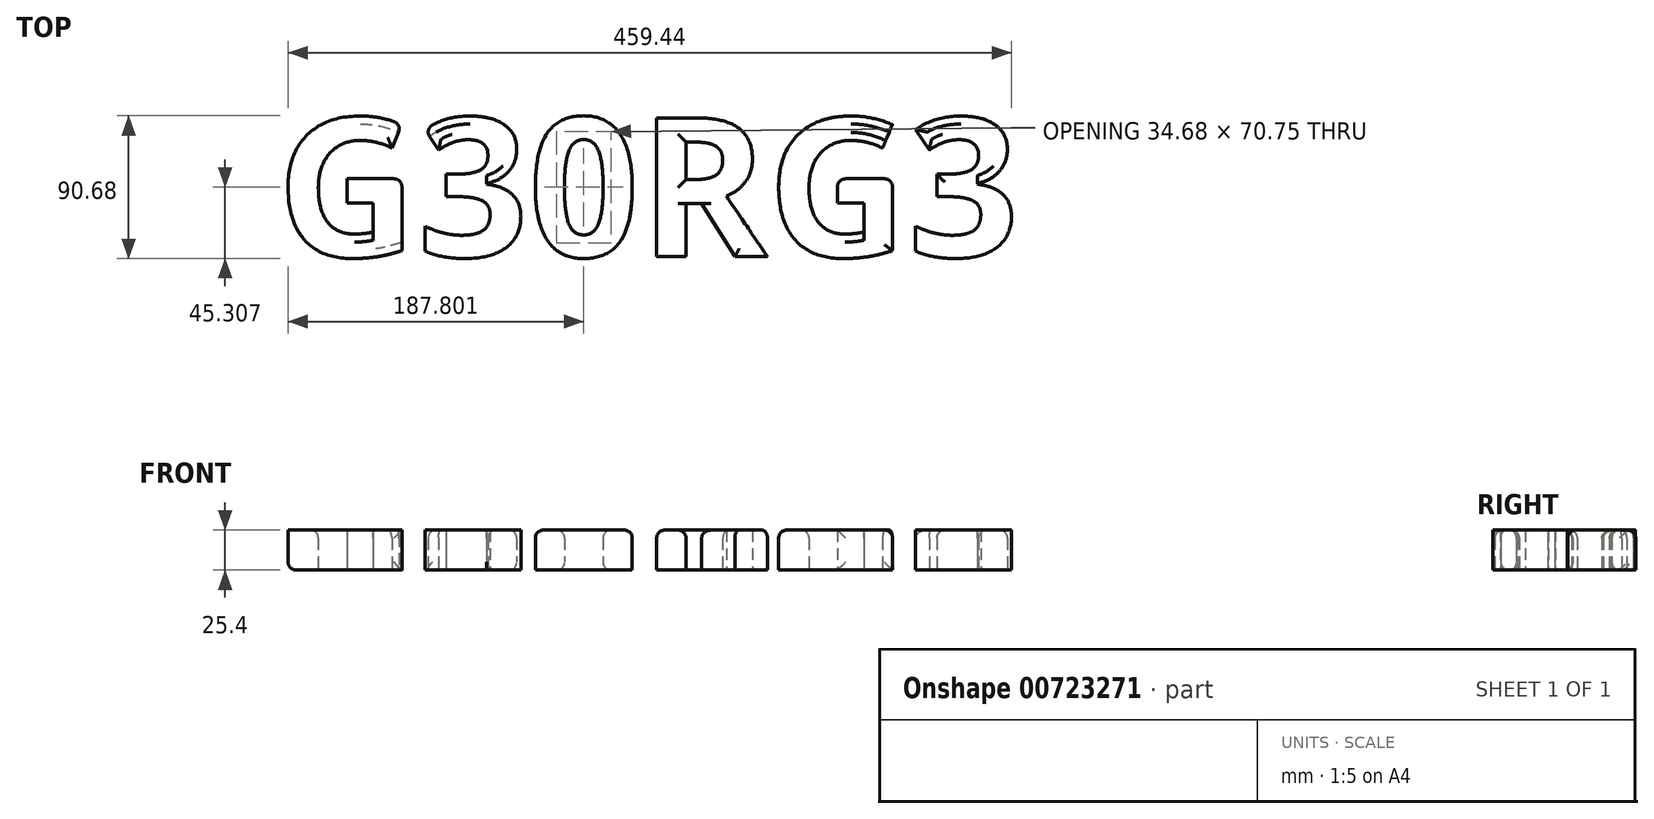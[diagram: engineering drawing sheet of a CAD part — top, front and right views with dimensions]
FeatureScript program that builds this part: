
annotation { "Feature Type Name" : "Feature", "Feature Type Description" : "" }
export const myFeature = defineFeature(function(context is Context, id is Id, definition is map)
    precondition{}
    {
        {
            var Q0;
            Q0=qCreatedBy(makeId("Top.planeOp"),FACE);
            var sketch = newSketch(context, id + "F0", { "sketchPlane" : qUnion([Q0])});
            skText(sketch, "E0", { "text": "G30RG3", "fontName": "OpenSans-Bold.ttf"});
            const initialGuessF0  = {"E0": [-0.20131, -0.08418, 1, 0, 0.08883]};
            skSetInitialGuess(sketch, initialGuessF0);
            skSolve(sketch);
        }
        {
            var Q0;
            Q0 = qSketchRegion(id + "F0", true);
            extrude(context, id + "F1", {"entities" : qUnion([Q0]), "depth" : 25.4 * mm, "offsetDistance" : 25.4 * mm});
        }
        {
            var Q0;
            Q0=makeQuery(id+"F1.opExtrude","CAP_EDGE",EDGE,{"disambiguationData":[OSD([sQuery(id+"F0.wireOp",EDGE,"E0.sketch_text.stroke-9")])],"isStart":false});
            var Q1;
            Q1=makeQuery(id+"F1.opExtrude","SWEPT_EDGE",EDGE,{"disambiguationData":[OSD([sQuery(id+"F0.wireOp",EDGE,"E0.sketch_text.stroke-8"),sQuery(id+"F0.wireOp",EDGE,"E0.sketch_text.stroke-9")])]});
            var Q2;
            Q2=makeQuery(id+"F1.opExtrude","CAP_EDGE",EDGE,{"disambiguationData":[OSD([sQuery(id+"F0.wireOp",EDGE,"E0.sketch_text.stroke-8")])],"isStart":true});
            var Q3;
            Q3=makeQuery(id+"F1.opExtrude","CAP_EDGE",EDGE,{"disambiguationData":[OSD([sQuery(id+"F0.wireOp",EDGE,"E0.sketch_text.stroke-10")])],"isStart":false});
            var Q4;
            Q4=makeQuery(id+"F1.opExtrude","CAP_EDGE",EDGE,{"disambiguationData":[OSD([sQuery(id+"F0.wireOp",EDGE,"E0.sketch_text.stroke-43")])],"isStart":false});
            var Q5;
            Q5=makeQuery(id+"F1.opExtrude","SWEPT_EDGE",EDGE,{"disambiguationData":[OSD([sQuery(id+"F0.wireOp",EDGE,"E0.sketch_text.stroke-42"),sQuery(id+"F0.wireOp",EDGE,"E0.sketch_text.stroke-43")])]});
            var Q6;
            Q6=makeQuery(id+"F1.opExtrude","CAP_EDGE",EDGE,{"disambiguationData":[OSD([sQuery(id+"F0.wireOp",EDGE,"E0.sketch_text.stroke-43")])],"isStart":true});
            var Q7;
            Q7=makeQuery(id+"F1.opExtrude","CAP_EDGE",EDGE,{"disambiguationData":[OSD([sQuery(id+"F0.wireOp",EDGE,"E0.sketch_text.stroke-42")])],"isStart":false});
            var Q8;
            Q8=makeQuery(id+"F1.opExtrude","CAP_EDGE",EDGE,{"disambiguationData":[OSD([sQuery(id+"F0.wireOp",EDGE,"E0.sketch_text.stroke-41")])],"isStart":false});
            var Q9;
            Q9=makeQuery(id+"F1.opExtrude","CAP_EDGE",EDGE,{"disambiguationData":[OSD([sQuery(id+"F0.wireOp",EDGE,"E0.sketch_text.stroke-0")])],"isStart":false});
            var Q10;
            Q10=makeQuery(id+"F1.opExtrude","CAP_EDGE",EDGE,{"disambiguationData":[OSD([sQuery(id+"F0.wireOp",EDGE,"E0.sketch_text.stroke-0")])],"isStart":true});
            var Q11;
            Q11=makeQuery(id+"F1.opExtrude","SWEPT_EDGE",EDGE,{"disambiguationData":[OSD([sQuery(id+"F0.wireOp",EDGE,"E0.sketch_text.stroke-0"),sQuery(id+"F0.wireOp",EDGE,"E0.sketch_text.stroke-1")])]});
            var Q12;
            Q12=makeQuery(id+"F1.opExtrude","CAP_EDGE",EDGE,{"disambiguationData":[OSD([sQuery(id+"F0.wireOp",EDGE,"E0.sketch_text.stroke-55")])],"isStart":false});
            var Q13;
            Q13=makeQuery(id+"F1.opExtrude","CAP_EDGE",EDGE,{"disambiguationData":[OSD([sQuery(id+"F0.wireOp",EDGE,"E0.sketch_text.stroke-55")])],"isStart":true});
            var Q14;
            Q14=makeQuery(id+"F1.opExtrude","CAP_EDGE",EDGE,{"disambiguationData":[OSD([sQuery(id+"F0.wireOp",EDGE,"E0.sketch_text.stroke-51")])],"isStart":false});
            var Q15;
            Q15=makeQuery(id+"F1.opExtrude","CAP_EDGE",EDGE,{"disambiguationData":[OSD([sQuery(id+"F0.wireOp",EDGE,"E0.sketch_text.stroke-52")])],"isStart":false});
            var Q16;
            Q16=makeQuery(id+"F1.opExtrude","CAP_EDGE",EDGE,{"disambiguationData":[OSD([sQuery(id+"F0.wireOp",EDGE,"E0.sketch_text.stroke-62")])],"isStart":false});
            var Q17;
            Q17=makeQuery(id+"F1.opExtrude","CAP_EDGE",EDGE,{"disambiguationData":[OSD([sQuery(id+"F0.wireOp",EDGE,"E0.sketch_text.stroke-68")])],"isStart":false});
            var Q18;
            Q18=makeQuery(id+"F1.opExtrude","CAP_EDGE",EDGE,{"disambiguationData":[OSD([sQuery(id+"F0.wireOp",EDGE,"E0.sketch_text.stroke-71")])],"isStart":false});
            var Q19;
            Q19=makeQuery(id+"F1.opExtrude","CAP_EDGE",EDGE,{"disambiguationData":[OSD([sQuery(id+"F0.wireOp",EDGE,"E0.sketch_text.stroke-69")])],"isStart":false});
            var Q20;
            Q20=makeQuery(id+"F1.opExtrude","CAP_EDGE",EDGE,{"disambiguationData":[OSD([sQuery(id+"F0.wireOp",EDGE,"E0.sketch_text.stroke-79")])],"isStart":false});
            var Q21;
            Q21=makeQuery(id+"F1.opExtrude","CAP_EDGE",EDGE,{"disambiguationData":[OSD([sQuery(id+"F0.wireOp",EDGE,"E0.sketch_text.stroke-78")])],"isStart":false});
            var Q22;
            Q22=makeQuery(id+"F1.opExtrude","CAP_EDGE",EDGE,{"disambiguationData":[OSD([sQuery(id+"F0.wireOp",EDGE,"E0.sketch_text.stroke-86")])],"isStart":false});
            var Q23;
            Q23=makeQuery(id+"F1.opExtrude","CAP_EDGE",EDGE,{"disambiguationData":[OSD([sQuery(id+"F0.wireOp",EDGE,"E0.sketch_text.stroke-87")])],"isStart":false});
            var Q24;
            Q24=makeQuery(id+"F1.opExtrude","CAP_EDGE",EDGE,{"disambiguationData":[OSD([sQuery(id+"F0.wireOp",EDGE,"E0.sketch_text.stroke-93")])],"isStart":false});
            var Q25;
            Q25=makeQuery(id+"F1.opExtrude","CAP_EDGE",EDGE,{"disambiguationData":[OSD([sQuery(id+"F0.wireOp",EDGE,"E0.sketch_text.stroke-92")])],"isStart":false});
            var Q26;
            Q26=makeQuery(id+"F1.opExtrude","CAP_EDGE",EDGE,{"disambiguationData":[OSD([sQuery(id+"F0.wireOp",EDGE,"E0.sketch_text.stroke-81")])],"isStart":false});
            var Q27;
            Q27=makeQuery(id+"F1.opExtrude","CAP_EDGE",EDGE,{"disambiguationData":[OSD([sQuery(id+"F0.wireOp",EDGE,"E0.sketch_text.stroke-81")])],"isStart":true});
            var Q28;
            Q28=makeQuery(id+"F1.opExtrude","SWEPT_EDGE",EDGE,{"disambiguationData":[OSD([sQuery(id+"F0.wireOp",EDGE,"E0.sketch_text.stroke-81"),sQuery(id+"F0.wireOp",EDGE,"E0.sketch_text.stroke-99")])]});
            var Q29;
            Q29=makeQuery(id+"F1.opExtrude","SWEPT_EDGE",EDGE,{"disambiguationData":[OSD([sQuery(id+"F0.wireOp",EDGE,"E0.sketch_text.stroke-81"),sQuery(id+"F0.wireOp",EDGE,"E0.sketch_text.stroke-82")])]});
            var Q30;
            Q30=makeQuery(id+"F1.opExtrude","CAP_EDGE",EDGE,{"disambiguationData":[OSD([sQuery(id+"F0.wireOp",EDGE,"E0.sketch_text.stroke-82")])],"isStart":false});
            var Q31;
            Q31=makeQuery(id+"F1.opExtrude","CAP_EDGE",EDGE,{"disambiguationData":[OSD([sQuery(id+"F0.wireOp",EDGE,"E0.sketch_text.stroke-116")])],"isStart":false});
            var Q32;
            Q32=makeQuery(id+"F1.opExtrude","CAP_EDGE",EDGE,{"disambiguationData":[OSD([sQuery(id+"F0.wireOp",EDGE,"E0.sketch_text.stroke-117")])],"isStart":false});
            var Q33;
            Q33=makeQuery(id+"F1.opExtrude","CAP_EDGE",EDGE,{"disambiguationData":[OSD([sQuery(id+"F0.wireOp",EDGE,"E0.sketch_text.stroke-118")])],"isStart":false});
            var Q34;
            Q34=makeQuery(id+"F1.opExtrude","CAP_EDGE",EDGE,{"disambiguationData":[OSD([sQuery(id+"F0.wireOp",EDGE,"E0.sketch_text.stroke-123")])],"isStart":false});
            var Q35;
            Q35=makeQuery(id+"F1.opExtrude","CAP_EDGE",EDGE,{"disambiguationData":[OSD([sQuery(id+"F0.wireOp",EDGE,"E0.sketch_text.stroke-124")])],"isStart":false});
            var Q36;
            Q36=makeQuery(id+"F1.opExtrude","CAP_EDGE",EDGE,{"disambiguationData":[OSD([sQuery(id+"F0.wireOp",EDGE,"E0.sketch_text.stroke-125")])],"isStart":false});
            var Q37;
            Q37=makeQuery(id+"F1.opExtrude","CAP_EDGE",EDGE,{"disambiguationData":[OSD([sQuery(id+"F0.wireOp",EDGE,"E0.sketch_text.stroke-126")])],"isStart":false});
            var Q38;
            Q38=makeQuery(id+"F1.opExtrude","CAP_EDGE",EDGE,{"disambiguationData":[OSD([sQuery(id+"F0.wireOp",EDGE,"E0.sketch_text.stroke-100")])],"isStart":false});
            fillet(context, id + "F2", {"entities" : qUnion([Q0, Q1, Q2, Q3, Q4, Q5, Q6, Q7, Q8, Q9, Q10, Q11, Q12, Q13, Q14, Q15, Q16, Q17, Q18, Q19, Q20, Q21, Q22, Q23, Q24, Q25, Q26, Q27, Q28, Q29, Q30, Q31, Q32, Q33, Q34, Q35, Q36, Q37, Q38]), "radius" : 5.08 * mm, "tangentPropagation" : true, "allowEdgeOverflow" : false});
        }
    });
